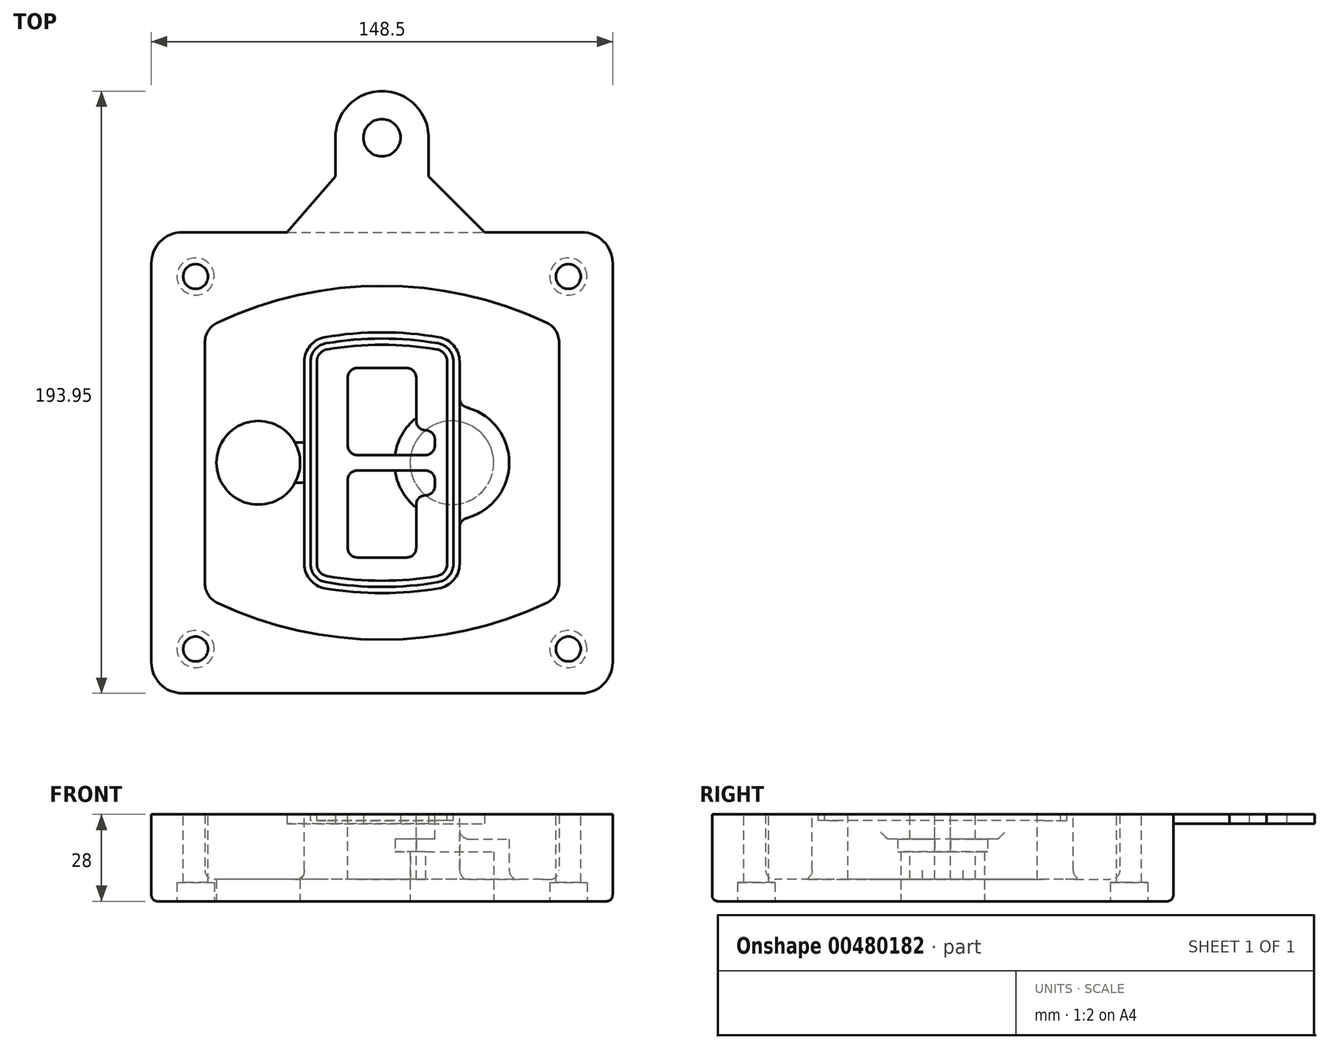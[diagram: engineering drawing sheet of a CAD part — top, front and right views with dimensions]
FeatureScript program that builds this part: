
annotation { "Feature Type Name" : "Feature", "Feature Type Description" : "" }
export const myFeature = defineFeature(function(context is Context, id is Id, definition is map)
    precondition{}
    {
        {
            var Q0;
            Q0=qCreatedBy(makeId("Top.planeOp"),FACE);
            var sketch = newSketch(context, id + "F0", { "sketchPlane" : qUnion([Q0])});
            skPoint(sketch, "E0.rect.middle", {"position": v(0, 0) * mm});
            skLineSegment(sketch, "E1.bottom", {"start": v(-64.25, -74.25) * mm, "end": v(64.25, -74.25) * mm});
            skLineSegment(sketch, "E1.top", {"start": v(-64.25, 74.25) * mm, "end": v(64.25, 74.25) * mm});
            skLineSegment(sketch, "E1.left", {"start": v(-74.25, -64.25) * mm, "end": v(-74.25, 64.25) * mm});
            skLineSegment(sketch, "E1.right", {"start": v(74.25, -64.25) * mm, "end": v(74.25, 64.25) * mm});
            skLineSegment(sketch, "E2", {"start": v(-74.25, 74.25) * mm, "end": v(74.25, -74.25) * mm, "construction": true});
            skLineSegment(sketch, "E3", {"start": v(74.25, 74.25) * mm, "end": v(-74.25, -74.25) * mm, "construction": true});
            skCircle(sketch, "E4", {"center": v(-60, 60) * mm, "radius": 4 * mm});
            skCircle(sketch, "E5", {"center": v(60, 60) * mm, "radius": 4 * mm});
            skCircle(sketch, "E6", {"center": v(60, -60) * mm, "radius": 4 * mm});
            skCircle(sketch, "E7", {"center": v(-60, -60) * mm, "radius": 4 * mm});
            skLineSegment(sketch, "E8", {"start": v(-60, 60) * mm, "end": v(60, 60) * mm, "construction": true});
            skLineSegment(sketch, "E9", {"start": v(60, 60) * mm, "end": v(60, -60) * mm, "construction": true});
            skLineSegment(sketch, "E10", {"start": v(60, -60) * mm, "end": v(-60, -60) * mm, "construction": true});
            skLineSegment(sketch, "E11", {"start": v(-60, -60) * mm, "end": v(-60, 60) * mm, "construction": true});
            skLineSegment(sketch, "E12", {"start": v(-60, 38.83) * mm, "end": v(-60, -38.83) * mm});
            skLineSegment(sketch, "E13", {"start": v(60, 38.83) * mm, "end": v(60, -38.83) * mm});
            skArc(sketch, "E14", {"start": v(54.26, 47.88) * mm, "mid": v(0, 60) * mm, "end": v(-54.26, 47.88) * mm});
            skArc(sketch, "E15", {"start": v(-54.26, -47.88) * mm, "mid": v(0, -60) * mm, "end": v(54.26, -47.88) * mm});
            skLineSegment(sketch, "E16", {"start": v(-60, 0) * mm, "end": v(60, 0) * mm, "construction": true});
            skPoint(sketch, "E17.visualSharp", {"position": v(-60, -45) * mm});
            skArc(sketch, "E17.filletArc", {"start": v(-60, -38.83) * mm, "mid": v(-58.44, -44.2) * mm, "end": v(-54.26, -47.88) * mm});
            skPoint(sketch, "E18.visualSharp", {"position": v(-60, 45) * mm});
            skArc(sketch, "E18.filletArc", {"start": v(-54.26, 47.88) * mm, "mid": v(-58.44, 44.2) * mm, "end": v(-60, 38.83) * mm});
            skPoint(sketch, "E19.visualSharp", {"position": v(60, 45) * mm});
            skArc(sketch, "E19.filletArc", {"start": v(60, 38.83) * mm, "mid": v(58.44, 44.2) * mm, "end": v(54.26, 47.88) * mm});
            skPoint(sketch, "E20.visualSharp", {"position": v(60, -45) * mm});
            skArc(sketch, "E20.filletArc", {"start": v(54.26, -47.88) * mm, "mid": v(58.44, -44.2) * mm, "end": v(60, -38.83) * mm});
            skPoint(sketch, "E21.visualSharp", {"position": v(-74.25, 74.25) * mm});
            skArc(sketch, "E21.filletArc", {"start": v(-64.25, 74.25) * mm, "mid": v(-71.32, 71.32) * mm, "end": v(-74.25, 64.25) * mm});
            skPoint(sketch, "E22.visualSharp", {"position": v(74.25, 74.25) * mm});
            skArc(sketch, "E22.filletArc", {"start": v(74.25, 64.25) * mm, "mid": v(71.32, 71.32) * mm, "end": v(64.25, 74.25) * mm});
            skPoint(sketch, "E23.visualSharp", {"position": v(74.25, -74.25) * mm});
            skArc(sketch, "E23.filletArc", {"start": v(64.25, -74.25) * mm, "mid": v(71.32, -71.32) * mm, "end": v(74.25, -64.25) * mm});
            skPoint(sketch, "E24.visualSharp", {"position": v(-74.25, -74.25) * mm});
            skArc(sketch, "E24.filletArc", {"start": v(-74.25, -64.25) * mm, "mid": v(-71.32, -71.32) * mm, "end": v(-64.25, -74.25) * mm});
            skArc(sketch, "E25.0", {"start": v(57, 38.83) * mm, "mid": v(55.9, 42.58) * mm, "end": v(52.98, 45.17) * mm});
            skLineSegment(sketch, "E25.1", {"start": v(57, 38.83) * mm, "end": v(57, -38.83) * mm});
            skArc(sketch, "E25.2", {"start": v(52.98, -45.17) * mm, "mid": v(55.9, -42.58) * mm, "end": v(57, -38.83) * mm});
            skArc(sketch, "E25.3", {"start": v(-52.98, -45.17) * mm, "mid": v(0, -57) * mm, "end": v(52.98, -45.17) * mm});
            skArc(sketch, "E25.4", {"start": v(-57, -38.83) * mm, "mid": v(-55.9, -42.58) * mm, "end": v(-52.98, -45.17) * mm});
            skArc(sketch, "E25.5", {"start": v(52.98, 45.17) * mm, "mid": v(0, 57) * mm, "end": v(-52.98, 45.17) * mm});
            skLineSegment(sketch, "E25.6", {"start": v(-57, 38.83) * mm, "end": v(-57, -38.83) * mm});
            skArc(sketch, "E25.7", {"start": v(-52.98, 45.17) * mm, "mid": v(-55.9, 42.58) * mm, "end": v(-57, 38.83) * mm});
            skArc(sketch, "E26.0", {"start": v(-55.96, 51.5) * mm, "mid": v(-61.82, 46.33) * mm, "end": v(-64, 38.83) * mm});
            skArc(sketch, "E26.1", {"start": v(55.96, 51.5) * mm, "mid": v(0, 64) * mm, "end": v(-55.96, 51.5) * mm});
            skArc(sketch, "E26.2", {"start": v(64, 38.83) * mm, "mid": v(61.82, 46.33) * mm, "end": v(55.96, 51.5) * mm});
            skLineSegment(sketch, "E26.3", {"start": v(64, 38.83) * mm, "end": v(64, -38.83) * mm});
            skArc(sketch, "E26.4", {"start": v(55.96, -51.5) * mm, "mid": v(61.82, -46.33) * mm, "end": v(64, -38.83) * mm});
            skLineSegment(sketch, "E26.5", {"start": v(-64, 38.83) * mm, "end": v(-64, -38.83) * mm});
            skArc(sketch, "E26.6", {"start": v(-55.96, -51.5) * mm, "mid": v(0, -64) * mm, "end": v(55.96, -51.5) * mm});
            skArc(sketch, "E26.7", {"start": v(-64, -38.83) * mm, "mid": v(-61.82, -46.33) * mm, "end": v(-55.96, -51.5) * mm});
            skSolve(sketch);
        }
        {
            var Q0;
            Q0=makeQuery(id+"F0.imprint","IMPRINT",FACE,{"disambiguationData":[TD([[makeQuery(id+"F0.imprint","IMPRINT",EDGE,{"derivedFrom":sQuery(id+"F0.wireOp",EDGE,"E1.bottom")}),1.0]])]});
            var Q1;
            Q1=makeQuery(id+"F0.imprint","IMPRINT",FACE,{"disambiguationData":[TD([[makeQuery(id+"F0.imprint","IMPRINT",EDGE,{"derivedFrom":sQuery(id+"F0.wireOp",EDGE,"E12")}),1.0]])]});
            var Q2;
            Q2=makeQuery(id+"F0.imprint","IMPRINT",FACE,{"disambiguationData":[TD([[makeQuery(id+"F0.imprint","IMPRINT",EDGE,{"derivedFrom":sQuery(id+"F0.wireOp",EDGE,"E25.0")}),1.0]])]});
            var Q3;
            Q3=makeQuery(id+"F0.imprint","IMPRINT",FACE,{"disambiguationData":[TD([[makeQuery(id+"F0.imprint","IMPRINT",EDGE,{"derivedFrom":sQuery(id+"F0.wireOp",EDGE,"E12")}),-1.0]])]});
            extrude(context, id + "F1", {"entities" : qUnion([Q0, Q1, Q2, Q3]), "oppositeDirection" : true, "depth" : 25 * mm});
        }
        {
            var Q0;
            Q0=makeQuery(id+"F0.imprint","IMPRINT",FACE,{"disambiguationData":[TD([[makeQuery(id+"F0.imprint","IMPRINT",EDGE,{"derivedFrom":sQuery(id+"F0.wireOp",EDGE,"E12")}),1.0]])]});
            extrude(context, id + "F2", {"entities" : qUnion([Q0]), "operationType" : NewBodyOperationType.ADD, "depth" : 3 * mm});
        }
        {
            var Q0;
            Q0=makeQuery(id+"F0.imprint","IMPRINT",FACE,{"disambiguationData":[TD([[makeQuery(id+"F0.imprint","IMPRINT",EDGE,{"derivedFrom":sQuery(id+"F0.wireOp",EDGE,"E25.0")}),1.0]])]});
            extrude(context, id + "F3", {"entities" : qUnion([Q0]), "operationType" : NewBodyOperationType.REMOVE, "oppositeDirection" : true, "depth" : 18 * mm});
        }
        {
            var Q0;
            Q0=makeQuery(id+"F2.opExtrude","CAP_FACE",FACE,{"disambiguationData":[OSD([sQuery(id+"F0.wireOp",EDGE,"E12"),sQuery(id+"F0.wireOp",EDGE,"E13"),sQuery(id+"F0.wireOp",EDGE,"E14"),sQuery(id+"F0.wireOp",EDGE,"E15"),sQuery(id+"F0.wireOp",EDGE,"E17.filletArc"),sQuery(id+"F0.wireOp",EDGE,"E18.filletArc"),sQuery(id+"F0.wireOp",EDGE,"E19.filletArc"),sQuery(id+"F0.wireOp",EDGE,"E20.filletArc"),sQuery(id+"F0.wireOp",EDGE,"E25.0"),sQuery(id+"F0.wireOp",EDGE,"E25.1"),sQuery(id+"F0.wireOp",EDGE,"E25.2"),sQuery(id+"F0.wireOp",EDGE,"E25.3"),sQuery(id+"F0.wireOp",EDGE,"E25.4"),sQuery(id+"F0.wireOp",EDGE,"E25.5"),sQuery(id+"F0.wireOp",EDGE,"E25.6"),sQuery(id+"F0.wireOp",EDGE,"E25.7")])],"isStart":false});
            var sketch = newSketch(context, id + "F4", { "sketchPlane" : qUnion([Q0])});
            skArc(sketch, "E27.0", {"start": v(-18.34, -40.45) * mm, "mid": v(0, -42) * mm, "end": v(18.34, -40.45) * mm});
            skArc(sketch, "E28.0", {"start": v(18.34, 40.45) * mm, "mid": v(0, 42) * mm, "end": v(-18.34, 40.45) * mm});
            skLineSegment(sketch, "E29", {"start": v(-25, 32.57) * mm, "end": v(-25, -32.57) * mm});
            skLineSegment(sketch, "E30", {"start": v(25, 32.57) * mm, "end": v(25, -32.57) * mm});
            skLineSegment(sketch, "E31", {"start": v(-25, 39.1) * mm, "end": v(25, 39.1) * mm, "construction": true});
            skLineSegment(sketch, "E32", {"start": v(-25, -39.1) * mm, "end": v(25, -39.1) * mm, "construction": true});
            skPoint(sketch, "E33.visualSharp", {"position": v(-25, 39.1) * mm});
            skArc(sketch, "E33.filletArc", {"start": v(-18.34, 40.45) * mm, "mid": v(-23.11, 37.73) * mm, "end": v(-25, 32.57) * mm});
            skPoint(sketch, "E34.visualSharp", {"position": v(25, 39.1) * mm});
            skArc(sketch, "E34.filletArc", {"start": v(25, 32.57) * mm, "mid": v(23.11, 37.73) * mm, "end": v(18.34, 40.45) * mm});
            skPoint(sketch, "E35.visualSharp", {"position": v(25, -39.1) * mm});
            skArc(sketch, "E35.filletArc", {"start": v(18.34, -40.45) * mm, "mid": v(23.11, -37.73) * mm, "end": v(25, -32.57) * mm});
            skPoint(sketch, "E36.visualSharp", {"position": v(-25, -39.1) * mm});
            skArc(sketch, "E36.filletArc", {"start": v(-25, -32.57) * mm, "mid": v(-23.11, -37.73) * mm, "end": v(-18.34, -40.45) * mm});
            skArc(sketch, "E37.0", {"start": v(52.98, 45.17) * mm, "mid": v(0, 57) * mm, "end": v(-52.98, 45.17) * mm});
            skArc(sketch, "E37.1", {"start": v(-52.98, 45.17) * mm, "mid": v(-55.9, 42.58) * mm, "end": v(-57, 38.83) * mm});
            skLineSegment(sketch, "E37.2", {"start": v(-57, 38.83) * mm, "end": v(-57, -38.83) * mm});
            skArc(sketch, "E37.3", {"start": v(-57, -38.83) * mm, "mid": v(-55.9, -42.58) * mm, "end": v(-52.98, -45.17) * mm});
            skArc(sketch, "E37.4", {"start": v(-52.98, -45.17) * mm, "mid": v(0, -57) * mm, "end": v(52.98, -45.17) * mm});
            skArc(sketch, "E37.5", {"start": v(52.98, -45.17) * mm, "mid": v(55.9, -42.58) * mm, "end": v(57, -38.83) * mm});
            skLineSegment(sketch, "E37.6", {"start": v(57, 38.83) * mm, "end": v(57, -38.83) * mm});
            skArc(sketch, "E37.7", {"start": v(57, 38.83) * mm, "mid": v(55.9, 42.58) * mm, "end": v(52.98, 45.17) * mm});
            skLineSegment(sketch, "E38.0", {"start": v(23, 32.57) * mm, "end": v(23, -32.57) * mm});
            skArc(sketch, "E38.1", {"start": v(18, -38.48) * mm, "mid": v(21.58, -36.44) * mm, "end": v(23, -32.57) * mm});
            skArc(sketch, "E38.2", {"start": v(-18, -38.48) * mm, "mid": v(0, -40) * mm, "end": v(18, -38.48) * mm});
            skArc(sketch, "E38.3", {"start": v(-23, -32.57) * mm, "mid": v(-21.58, -36.44) * mm, "end": v(-18, -38.48) * mm});
            skLineSegment(sketch, "E38.4", {"start": v(-23, 32.57) * mm, "end": v(-23, -32.57) * mm});
            skArc(sketch, "E38.5", {"start": v(23, 32.57) * mm, "mid": v(21.58, 36.44) * mm, "end": v(18, 38.48) * mm});
            skArc(sketch, "E38.6", {"start": v(-18, 38.48) * mm, "mid": v(-21.58, 36.44) * mm, "end": v(-23, 32.57) * mm});
            skArc(sketch, "E38.7", {"start": v(18, 38.48) * mm, "mid": v(0, 40) * mm, "end": v(-18, 38.48) * mm});
            skArc(sketch, "E39.0", {"start": v(21, 32.57) * mm, "mid": v(20.06, 35.15) * mm, "end": v(17.67, 36.5) * mm});
            skLineSegment(sketch, "E39.1", {"start": v(21, 32.57) * mm, "end": v(21, -32.57) * mm});
            skArc(sketch, "E39.2", {"start": v(17.67, -36.5) * mm, "mid": v(20.06, -35.15) * mm, "end": v(21, -32.57) * mm});
            skArc(sketch, "E39.3", {"start": v(-17.67, -36.5) * mm, "mid": v(0, -38) * mm, "end": v(17.67, -36.5) * mm});
            skArc(sketch, "E39.4", {"start": v(-21, -32.57) * mm, "mid": v(-20.06, -35.15) * mm, "end": v(-17.67, -36.5) * mm});
            skArc(sketch, "E39.5", {"start": v(17.67, 36.5) * mm, "mid": v(0, 38) * mm, "end": v(-17.67, 36.5) * mm});
            skLineSegment(sketch, "E39.6", {"start": v(-21, 32.57) * mm, "end": v(-21, -32.57) * mm});
            skArc(sketch, "E39.7", {"start": v(-17.67, 36.5) * mm, "mid": v(-20.06, 35.15) * mm, "end": v(-21, 32.57) * mm});
            skLineSegment(sketch, "E40", {"start": v(-25, 0) * mm, "end": v(25, 0) * mm, "construction": true});
            skLineSegment(sketch, "E41", {"start": v(-11, 5.5) * mm, "end": v(-11, 27.5) * mm});
            skLineSegment(sketch, "E42", {"start": v(-8, 30.5) * mm, "end": v(8, 30.5) * mm});
            skLineSegment(sketch, "E43", {"start": v(11, 27.5) * mm, "end": v(11, 13.5) * mm});
            skLineSegment(sketch, "E44", {"start": v(14, 10.5) * mm, "end": v(14, 10.5) * mm});
            skLineSegment(sketch, "E45", {"start": v(17, 7.5) * mm, "end": v(17, 5.5) * mm});
            skLineSegment(sketch, "E46", {"start": v(14, 2.5) * mm, "end": v(-8, 2.5) * mm});
            skPoint(sketch, "E47.visualSharp", {"position": v(-11, 30.5) * mm});
            skArc(sketch, "E47.filletArc", {"start": v(-8, 30.5) * mm, "mid": v(-10.12, 29.62) * mm, "end": v(-11, 27.5) * mm});
            skPoint(sketch, "E48.visualSharp", {"position": v(11, 30.5) * mm});
            skArc(sketch, "E48.filletArc", {"start": v(11, 27.5) * mm, "mid": v(10.12, 29.62) * mm, "end": v(8, 30.5) * mm});
            skPoint(sketch, "E49.visualSharp", {"position": v(11, 10.5) * mm});
            skArc(sketch, "E49.filletArc", {"start": v(11, 13.5) * mm, "mid": v(11.88, 11.38) * mm, "end": v(14, 10.5) * mm});
            skPoint(sketch, "E50.visualSharp", {"position": v(17, 10.5) * mm});
            skArc(sketch, "E50.filletArc", {"start": v(17, 7.5) * mm, "mid": v(16.12, 9.62) * mm, "end": v(14, 10.5) * mm});
            skPoint(sketch, "E51.visualSharp", {"position": v(17, 2.5) * mm});
            skArc(sketch, "E51.filletArc", {"start": v(14, 2.5) * mm, "mid": v(16.12, 3.38) * mm, "end": v(17, 5.5) * mm});
            skPoint(sketch, "E52.visualSharp", {"position": v(-11, 2.5) * mm});
            skArc(sketch, "E52.filletArc", {"start": v(-11, 5.5) * mm, "mid": v(-10.12, 3.38) * mm, "end": v(-8, 2.5) * mm});
            skLineSegment(sketch, "E53.0.MirrorCS", {"start": v(14, -2.5) * mm, "end": v(-8, -2.5) * mm});
            skArc(sketch, "E54.0.MirrorCS", {"start": v(-11, -5.5) * mm, "mid": v(-10.12, -3.38) * mm, "end": v(-8, -2.5) * mm});
            skLineSegment(sketch, "E55.0.MirrorCS", {"start": v(-11, -5.5) * mm, "end": v(-11, -27.5) * mm});
            skArc(sketch, "E56.0.MirrorCS", {"start": v(-8, -30.5) * mm, "mid": v(-10.12, -29.62) * mm, "end": v(-11, -27.5) * mm});
            skLineSegment(sketch, "E57.0.MirrorCS", {"start": v(-8, -30.5) * mm, "end": v(8, -30.5) * mm});
            skArc(sketch, "E58.0.MirrorCS", {"start": v(11, -27.5) * mm, "mid": v(10.12, -29.62) * mm, "end": v(8, -30.5) * mm});
            skLineSegment(sketch, "E59.0.MirrorCS", {"start": v(11, -27.5) * mm, "end": v(11, -13.5) * mm});
            skArc(sketch, "E60.0.MirrorCS", {"start": v(11, -13.5) * mm, "mid": v(11.88, -11.38) * mm, "end": v(14, -10.5) * mm});
            skArc(sketch, "E61.0.MirrorCS", {"start": v(17, -7.5) * mm, "mid": v(16.12, -9.62) * mm, "end": v(14, -10.5) * mm});
            skLineSegment(sketch, "E62.0.MirrorCS", {"start": v(17, -7.5) * mm, "end": v(17, -5.5) * mm});
            skArc(sketch, "E63.0.MirrorCS", {"start": v(14, -2.5) * mm, "mid": v(16.12, -3.38) * mm, "end": v(17, -5.5) * mm});
            skSolve(sketch);
        }
        {
            var Q0;
            Q0=makeQuery(id+"F4.imprint","IMPRINT",FACE,{"disambiguationData":[TD([[makeQuery(id+"F4.imprint","IMPRINT",EDGE,{"derivedFrom":sQuery(id+"F4.wireOp",EDGE,"E27.0")}),1.0]])]});
            var Q1;
            Q1=makeQuery(id+"F4.imprint","IMPRINT",FACE,{"disambiguationData":[TD([[makeQuery(id+"F4.imprint","IMPRINT",EDGE,{"derivedFrom":sQuery(id+"F4.wireOp",EDGE,"E38.0")}),-1.0]])]});
            var Q2;
            Q2=makeQuery(id+"F4.imprint","IMPRINT",FACE,{"disambiguationData":[TD([[makeQuery(id+"F4.imprint","IMPRINT",EDGE,{"derivedFrom":sQuery(id+"F4.wireOp",EDGE,"E39.0")}),1.0]])]});
            extrude(context, id + "F5", {"entities" : qUnion([Q0, Q1, Q2]), "operationType" : NewBodyOperationType.ADD, "endBound" : BoundingType.UP_TO_NEXT, "oppositeDirection" : true, "depth" : 25 * mm});
        }
        {
            var Q0;
            Q0=makeQuery(id+"F4.imprint","IMPRINT",FACE,{"disambiguationData":[TD([[makeQuery(id+"F4.imprint","IMPRINT",EDGE,{"derivedFrom":sQuery(id+"F4.wireOp",EDGE,"E38.0")}),-1.0]])]});
            extrude(context, id + "F6", {"entities" : qUnion([Q0]), "operationType" : NewBodyOperationType.REMOVE, "oppositeDirection" : true, "depth" : 2 * mm});
        }
        {
            var Q0;
            Q0=makeQuery(id+"F1.opExtrude","CAP_FACE",FACE,{"disambiguationData":[OSD([sQuery(id+"F0.wireOp",EDGE,"E1.bottom"),sQuery(id+"F0.wireOp",EDGE,"E1.top"),sQuery(id+"F0.wireOp",EDGE,"E1.left"),sQuery(id+"F0.wireOp",EDGE,"E1.right"),sQuery(id+"F0.wireOp",EDGE,"E4"),sQuery(id+"F0.wireOp",EDGE,"E5"),sQuery(id+"F0.wireOp",EDGE,"E6"),sQuery(id+"F0.wireOp",EDGE,"E7"),sQuery(id+"F0.wireOp",EDGE,"E21.filletArc"),sQuery(id+"F0.wireOp",EDGE,"E22.filletArc"),sQuery(id+"F0.wireOp",EDGE,"E23.filletArc"),sQuery(id+"F0.wireOp",EDGE,"E24.filletArc")])],"isStart":false});
            var sketch = newSketch(context, id + "F7", { "sketchPlane" : qUnion([Q0])});
            skCircle(sketch, "E64", {"center": v(22.5, 0) * mm, "radius": 13.47 * mm});
            skCircle(sketch, "E65", {"center": v(-39.81, 0) * mm, "radius": 13.47 * mm});
            skLineSegment(sketch, "E66", {"start": v(74.25, 0) * mm, "end": v(-74.25, 0) * mm});
            skCircle(sketch, "E67", {"center": v(22.5, 0) * mm, "radius": 18.47 * mm});
            skCircle(sketch, "E68", {"center": v(60, -60) * mm, "radius": 6 * mm});
            skCircle(sketch, "E69", {"center": v(-60, -60) * mm, "radius": 6 * mm});
            skCircle(sketch, "E70", {"center": v(-60, 60) * mm, "radius": 6 * mm});
            skCircle(sketch, "E71", {"center": v(60, 60) * mm, "radius": 6 * mm});
            skSolve(sketch);
        }
        {
            var Q0;
            {var subQ1=sQuery(id+"F7.wireOp",EDGE,"E66");var subQ4=sQuery(id+"F7.wireOp",EDGE,"E64");var subQ6=makeQuery(id+"F7.imprint","INTERSECT",VERTEX,{"disambiguationData":[OD(0.0)],"derivedFrom":[subQ4,subQ1]});Q0=makeQuery(id+"F7.imprint","IMPRINT",FACE,{"disambiguationData":[TD([[makeQuery(id+"F7.imprint","IMPRINT",EDGE,{"disambiguationData":[TD([[subQ6,-1.0]])],"derivedFrom":subQ4}),-1.0]])]});}
            var Q1;
            {var subQ0=sQuery(id+"F7.wireOp",EDGE,"E66");var subQ1=sQuery(id+"F7.wireOp",EDGE,"E64");var subQ3=makeQuery(id+"F7.imprint","INTERSECT",VERTEX,{"disambiguationData":[OD(0.0)],"derivedFrom":[subQ1,subQ0]});Q1=makeQuery(id+"F7.imprint","IMPRINT",FACE,{"disambiguationData":[TD([[makeQuery(id+"F7.imprint","IMPRINT",EDGE,{"disambiguationData":[TD([[subQ3,-1.0]])],"derivedFrom":subQ1}),1.0]])]});}
            var Q2;
            {var subQ0=sQuery(id+"F7.wireOp",EDGE,"E66");var subQ1=sQuery(id+"F7.wireOp",EDGE,"E64");var subQ3=makeQuery(id+"F7.imprint","INTERSECT",VERTEX,{"disambiguationData":[OD(0.0)],"derivedFrom":[subQ1,subQ0]});Q2=makeQuery(id+"F7.imprint","IMPRINT",FACE,{"disambiguationData":[TD([[makeQuery(id+"F7.imprint","IMPRINT",EDGE,{"disambiguationData":[TD([[subQ3,1.0]])],"derivedFrom":subQ1}),1.0]])]});}
            var Q3;
            {var subQ1=sQuery(id+"F7.wireOp",EDGE,"E66");var subQ4=sQuery(id+"F7.wireOp",EDGE,"E64");var subQ6=makeQuery(id+"F7.imprint","INTERSECT",VERTEX,{"disambiguationData":[OD(0.0)],"derivedFrom":[subQ4,subQ1]});Q3=makeQuery(id+"F7.imprint","IMPRINT",FACE,{"disambiguationData":[TD([[makeQuery(id+"F7.imprint","IMPRINT",EDGE,{"disambiguationData":[TD([[subQ6,1.0]])],"derivedFrom":subQ4}),-1.0]])]});}
            extrude(context, id + "F8", {"entities" : qUnion([Q0, Q1, Q2, Q3]), "operationType" : NewBodyOperationType.ADD, "oppositeDirection" : true, "depth" : 20 * mm});
        }
        {
            var Q0;
            {var subQ0=sQuery(id+"F7.wireOp",EDGE,"E66");var subQ1=sQuery(id+"F7.wireOp",EDGE,"E64");var subQ3=makeQuery(id+"F7.imprint","INTERSECT",VERTEX,{"disambiguationData":[OD(0.0)],"derivedFrom":[subQ1,subQ0]});Q0=makeQuery(id+"F7.imprint","IMPRINT",FACE,{"disambiguationData":[TD([[makeQuery(id+"F7.imprint","IMPRINT",EDGE,{"disambiguationData":[TD([[subQ3,-1.0]])],"derivedFrom":subQ1}),1.0]])]});}
            var Q1;
            {var subQ0=sQuery(id+"F7.wireOp",EDGE,"E66");var subQ1=sQuery(id+"F7.wireOp",EDGE,"E64");var subQ3=makeQuery(id+"F7.imprint","INTERSECT",VERTEX,{"disambiguationData":[OD(0.0)],"derivedFrom":[subQ1,subQ0]});Q1=makeQuery(id+"F7.imprint","IMPRINT",FACE,{"disambiguationData":[TD([[makeQuery(id+"F7.imprint","IMPRINT",EDGE,{"disambiguationData":[TD([[subQ3,1.0]])],"derivedFrom":subQ1}),1.0]])]});}
            extrude(context, id + "F9", {"entities" : qUnion([Q0, Q1]), "operationType" : NewBodyOperationType.REMOVE, "oppositeDirection" : true, "depth" : 16 * mm});
        }
        {
            var Q0;
            {var subQ0=sQuery(id+"F7.wireOp",EDGE,"E66");var subQ1=sQuery(id+"F7.wireOp",EDGE,"E65");var subQ3=makeQuery(id+"F7.imprint","INTERSECT",VERTEX,{"disambiguationData":[OD(0.0)],"derivedFrom":[subQ1,subQ0]});Q0=makeQuery(id+"F7.imprint","IMPRINT",FACE,{"disambiguationData":[TD([[makeQuery(id+"F7.imprint","IMPRINT",EDGE,{"disambiguationData":[TD([[subQ3,-1.0]])],"derivedFrom":subQ1}),1.0]])]});}
            var Q1;
            {var subQ0=sQuery(id+"F7.wireOp",EDGE,"E66");var subQ1=sQuery(id+"F7.wireOp",EDGE,"E65");var subQ3=makeQuery(id+"F7.imprint","INTERSECT",VERTEX,{"disambiguationData":[OD(0.0)],"derivedFrom":[subQ1,subQ0]});Q1=makeQuery(id+"F7.imprint","IMPRINT",FACE,{"disambiguationData":[TD([[makeQuery(id+"F7.imprint","IMPRINT",EDGE,{"disambiguationData":[TD([[subQ3,1.0]])],"derivedFrom":subQ1}),1.0]])]});}
            extrude(context, id + "F10", {"entities" : qUnion([Q0, Q1]), "operationType" : NewBodyOperationType.REMOVE, "oppositeDirection" : true, "depth" : 25 * mm});
        }
        {
            var Q0;
            Q0=makeQuery(id+"F7.imprint","IMPRINT",FACE,{"disambiguationData":[TD([[makeQuery(id+"F7.imprint","IMPRINT",EDGE,{"derivedFrom":sQuery(id+"F7.wireOp",EDGE,"E68")}),1.0]])]});
            var Q1;
            Q1=makeQuery(id+"F7.imprint","IMPRINT",FACE,{"disambiguationData":[TD([[makeQuery(id+"F7.imprint","IMPRINT",EDGE,{"derivedFrom":makeQuery(id+"F1.opExtrude","CAP_EDGE",EDGE,{"disambiguationData":[OSD([sQuery(id+"F0.wireOp",EDGE,"E5")])],"isStart":false})}),-1.0]])]});
            var Q2;
            Q2=makeQuery(id+"F7.imprint","IMPRINT",FACE,{"disambiguationData":[TD([[makeQuery(id+"F7.imprint","IMPRINT",EDGE,{"derivedFrom":sQuery(id+"F7.wireOp",EDGE,"E69")}),1.0]])]});
            var Q3;
            Q3=makeQuery(id+"F7.imprint","IMPRINT",FACE,{"disambiguationData":[TD([[makeQuery(id+"F7.imprint","IMPRINT",EDGE,{"derivedFrom":makeQuery(id+"F1.opExtrude","CAP_EDGE",EDGE,{"disambiguationData":[OSD([sQuery(id+"F0.wireOp",EDGE,"E4")])],"isStart":false})}),-1.0]])]});
            var Q4;
            Q4=makeQuery(id+"F7.imprint","IMPRINT",FACE,{"disambiguationData":[TD([[makeQuery(id+"F7.imprint","IMPRINT",EDGE,{"derivedFrom":sQuery(id+"F7.wireOp",EDGE,"E70")}),1.0]])]});
            var Q5;
            Q5=makeQuery(id+"F7.imprint","IMPRINT",FACE,{"disambiguationData":[TD([[makeQuery(id+"F7.imprint","IMPRINT",EDGE,{"derivedFrom":makeQuery(id+"F1.opExtrude","CAP_EDGE",EDGE,{"disambiguationData":[OSD([sQuery(id+"F0.wireOp",EDGE,"E7")])],"isStart":false})}),-1.0]])]});
            var Q6;
            Q6=makeQuery(id+"F7.imprint","IMPRINT",FACE,{"disambiguationData":[TD([[makeQuery(id+"F7.imprint","IMPRINT",EDGE,{"derivedFrom":sQuery(id+"F7.wireOp",EDGE,"E71")}),1.0]])]});
            var Q7;
            Q7=makeQuery(id+"F7.imprint","IMPRINT",FACE,{"disambiguationData":[TD([[makeQuery(id+"F7.imprint","IMPRINT",EDGE,{"derivedFrom":makeQuery(id+"F1.opExtrude","CAP_EDGE",EDGE,{"disambiguationData":[OSD([sQuery(id+"F0.wireOp",EDGE,"E6")])],"isStart":false})}),-1.0]])]});
            extrude(context, id + "F11", {"entities" : qUnion([Q0, Q1, Q2, Q3, Q4, Q5, Q6, Q7]), "operationType" : NewBodyOperationType.REMOVE, "oppositeDirection" : true, "depth" : 6 * mm});
        }
        {
            var Q0;
            Q0=makeQuery(id+"F9.boolean.opBoolean","COPY",FACE,{"derivedFrom":makeQuery(id+"F9.opExtrude","CAP_FACE",FACE,{"disambiguationData":[OSD([sQuery(id+"F7.wireOp",EDGE,"E64")])],"isStart":false})});
            var sketch = newSketch(context, id + "F12", { "sketchPlane" : qUnion([Q0])});
            skArc(sketch, "E72.0", {"start": v(11, 14.45) * mm, "mid": v(6.45, 9.13) * mm, "end": v(4.2, 2.5) * mm});
            skArc(sketch, "E72.1", {"start": v(4.2, -2.5) * mm, "mid": v(6.45, -9.13) * mm, "end": v(11, -14.45) * mm});
            skLineSegment(sketch, "E73", {"start": v(4.2, -2.5) * mm, "end": v(14, -2.5) * mm});
            skLineSegment(sketch, "E74.0", {"start": v(14, 2.5) * mm, "end": v(4.2, 2.5) * mm});
            skArc(sketch, "E74.1", {"start": v(14, 2.5) * mm, "mid": v(16.12, 3.38) * mm, "end": v(17, 5.5) * mm});
            skLineSegment(sketch, "E74.2", {"start": v(17, 7.5) * mm, "end": v(17, 5.5) * mm});
            skArc(sketch, "E74.3", {"start": v(17, 7.5) * mm, "mid": v(16.12, 9.62) * mm, "end": v(14, 10.5) * mm});
            skArc(sketch, "E74.4", {"start": v(11, 13.5) * mm, "mid": v(11.88, 11.38) * mm, "end": v(14, 10.5) * mm});
            skLineSegment(sketch, "E74.5", {"start": v(11, 14.45) * mm, "end": v(11, 13.5) * mm});
            skLineSegment(sketch, "E74.7", {"start": v(14, -2.5) * mm, "end": v(4.2, -2.5) * mm});
            skArc(sketch, "E74.8", {"start": v(14, -2.5) * mm, "mid": v(16.12, -3.38) * mm, "end": v(17, -5.5) * mm});
            skLineSegment(sketch, "E74.9", {"start": v(17, -7.5) * mm, "end": v(17, -5.5) * mm});
            skArc(sketch, "E74.10", {"start": v(17, -7.5) * mm, "mid": v(16.12, -9.62) * mm, "end": v(14, -10.5) * mm});
            skArc(sketch, "E74.11", {"start": v(11, -13.5) * mm, "mid": v(11.88, -11.38) * mm, "end": v(14, -10.5) * mm});
            skLineSegment(sketch, "E74.12", {"start": v(11, -14.45) * mm, "end": v(11, -13.5) * mm});
            skPoint(sketch, "E75.orphan", {"position": v(11, -27.5) * mm});
            skPoint(sketch, "E76.orphan", {"position": v(-8, -2.5) * mm});
            skPoint(sketch, "E77.orphan", {"position": v(-8, 2.5) * mm});
            skPoint(sketch, "E78.orphan", {"position": v(11, 27.5) * mm});
            skSolve(sketch);
        }
        {
            var Q0;
            {var subQ7=sQuery(id+"F12.wireOp",EDGE,"E72.0");var subQ14=sQuery(id+"F12.wireOp",EDGE,"E72.1");var subQ16=sQuery(id+"F12.wireOp",EDGE,"E74.1");var subQ18=sQuery(id+"F12.wireOp",EDGE,"E74.8");Q0=qUnion([makeQuery(id+"F12.imprint","IMPRINT",FACE,{"disambiguationData":[TD([[makeQuery(id+"F12.imprint","IMPRINT",EDGE,{"derivedFrom":subQ7}),1.0]])]}),makeQuery(id+"F12.imprint","IMPRINT",FACE,{"disambiguationData":[TD([[makeQuery(id+"F12.imprint","IMPRINT",EDGE,{"derivedFrom":subQ14}),1.0]])]}),makeQuery(id+"F12.imprint","IMPRINT",FACE,{"disambiguationData":[TD([[makeQuery(id+"F12.imprint","IMPRINT",EDGE,{"derivedFrom":subQ16}),1.0]])]}),makeQuery(id+"F12.imprint","IMPRINT",FACE,{"disambiguationData":[TD([[makeQuery(id+"F12.imprint","IMPRINT",EDGE,{"derivedFrom":subQ18}),-1.0]])]})]);}
            var Q1;
            Q1=makeQuery(id+"F5.boolean.opBoolean","SPLIT",FACE,{"disambiguationData":[TD([makeQuery(id+"F5.opExtrude","SWEPT_FACE",FACE,{"disambiguationData":[OSD([sQuery(id+"F4.wireOp",EDGE,"E41")])]})])],"derivedFrom":makeQuery(id+"F3.boolean.opBoolean","COPY",FACE,{"derivedFrom":makeQuery(id+"F3.opExtrude","CAP_FACE",FACE,{"disambiguationData":[OSD([sQuery(id+"F0.wireOp",EDGE,"E25.0"),sQuery(id+"F0.wireOp",EDGE,"E25.1"),sQuery(id+"F0.wireOp",EDGE,"E25.2"),sQuery(id+"F0.wireOp",EDGE,"E25.3"),sQuery(id+"F0.wireOp",EDGE,"E25.4"),sQuery(id+"F0.wireOp",EDGE,"E25.5"),sQuery(id+"F0.wireOp",EDGE,"E25.6"),sQuery(id+"F0.wireOp",EDGE,"E25.7")])],"isStart":false})})});
            extrude(context, id + "F13", {"entities" : qUnion([Q0]), "operationType" : NewBodyOperationType.REMOVE, "endBound" : BoundingType.UP_TO_SURFACE, "endBoundEntityFace" : qUnion([Q1]), "depth" : 25 * mm});
        }
        {
            var Q0;
            Q0=makeQuery(id+"F3.boolean.opBoolean","COPY",EDGE,{"derivedFrom":makeQuery(id+"F3.opExtrude","CAP_EDGE",EDGE,{"disambiguationData":[OSD([sQuery(id+"F0.wireOp",EDGE,"E25.6")])],"isStart":false})});
            var Q1;
            Q1=makeQuery(id+"F8.boolean.opBoolean","INTERSECT",EDGE,{"derivedFrom":[makeQuery(id+"F5.opExtrude","SWEPT_FACE",FACE,{"disambiguationData":[OSD([sQuery(id+"F4.wireOp",EDGE,"E30")])]}),makeQuery(id+"F8.opExtrude","CAP_FACE",FACE,{"disambiguationData":[OSD([sQuery(id+"F7.wireOp",EDGE,"E67")])],"isStart":false})]});
            var Q2;
            Q2=makeQuery(id+"F8.boolean.opBoolean","INTERSECT",EDGE,{"disambiguationData":[OD(1.0)],"derivedFrom":[makeQuery(id+"F5.opExtrude","SWEPT_FACE",FACE,{"disambiguationData":[OSD([sQuery(id+"F4.wireOp",EDGE,"E30")])]}),makeQuery(id+"F8.opExtrude","SWEPT_FACE",FACE,{"disambiguationData":[OSD([sQuery(id+"F7.wireOp",EDGE,"E67")])]})]});
            var Q3;
            {var subQ0=sQuery(id+"F4.wireOp",EDGE,"E30");Q3=makeQuery(id+"F8.boolean.opBoolean","SPLIT",EDGE,{"disambiguationData":[TD([makeQuery(id+"F5.opExtrude","SWEPT_FACE",FACE,{"disambiguationData":[OSD([sQuery(id+"F4.wireOp",EDGE,"E35.filletArc")])]})])],"derivedFrom":makeQuery(id+"F5.opExtrude","CAP_EDGE",EDGE,{"disambiguationData":[OSD([subQ0])],"isStart":false})});}
            var Q4;
            {var subQ0=sQuery(id+"F0.wireOp",EDGE,"E25.7");var subQ1=sQuery(id+"F0.wireOp",EDGE,"E25.1");var subQ2=sQuery(id+"F0.wireOp",EDGE,"E25.6");var subQ3=sQuery(id+"F0.wireOp",EDGE,"E25.5");var subQ4=sQuery(id+"F0.wireOp",EDGE,"E25.4");var subQ5=sQuery(id+"F0.wireOp",EDGE,"E25.0");var subQ6=sQuery(id+"F0.wireOp",EDGE,"E25.2");var subQ7=sQuery(id+"F0.wireOp",EDGE,"E25.3");Q4=makeQuery(id+"F8.boolean.opBoolean","INTERSECT",EDGE,{"derivedFrom":[makeQuery(id+"F5.boolean.opBoolean","SPLIT",FACE,{"disambiguationData":[TD([makeQuery(id+"F2.opExtrude","SWEPT_FACE",FACE,{"disambiguationData":[OSD([subQ5])]})])],"derivedFrom":makeQuery(id+"F3.boolean.opBoolean","COPY",FACE,{"derivedFrom":makeQuery(id+"F3.opExtrude","CAP_FACE",FACE,{"disambiguationData":[OSD([subQ5,subQ1,subQ6,subQ7,subQ4,subQ3,subQ2,subQ0])],"isStart":false})})}),makeQuery(id+"F8.opExtrude","SWEPT_FACE",FACE,{"disambiguationData":[OSD([sQuery(id+"F7.wireOp",EDGE,"E67")])]})]});}
            var Q5;
            Q5=makeQuery(id+"F8.boolean.opBoolean","INTERSECT",EDGE,{"disambiguationData":[OD(0.0)],"derivedFrom":[makeQuery(id+"F5.opExtrude","SWEPT_FACE",FACE,{"disambiguationData":[OSD([sQuery(id+"F4.wireOp",EDGE,"E30")])]}),makeQuery(id+"F8.opExtrude","SWEPT_FACE",FACE,{"disambiguationData":[OSD([sQuery(id+"F7.wireOp",EDGE,"E67")])]})]});
            fillet(context, id + "F14", {"entities" : qUnion([Q0, Q1, Q2, Q3, Q4, Q5]), "radius" : 3 * mm, "tangentPropagation" : true, "allowEdgeOverflow" : false});
        }
        {
            var Q0;
            Q0=makeQuery(id+"F1.opExtrude","CAP_EDGE",EDGE,{"disambiguationData":[OSD([sQuery(id+"F0.wireOp",EDGE,"E1.bottom")])],"isStart":false});
            fillet(context, id + "F15", {"entities" : qUnion([Q0]), "radius" : 2 * mm, "tangentPropagation" : true, "allowEdgeOverflow" : false});
        }
        {
            var Q0;
            {var subQ0=sQuery(id+"F0.wireOp",EDGE,"E21.filletArc");var subQ1=sQuery(id+"F0.wireOp",EDGE,"E7");var subQ2=sQuery(id+"F0.wireOp",EDGE,"E6");var subQ3=sQuery(id+"F0.wireOp",EDGE,"E5");var subQ4=sQuery(id+"F0.wireOp",EDGE,"E4");var subQ5=sQuery(id+"F0.wireOp",EDGE,"E22.filletArc");var subQ6=sQuery(id+"F0.wireOp",EDGE,"E1.bottom");var subQ7=sQuery(id+"F0.wireOp",EDGE,"E1.right");var subQ8=sQuery(id+"F0.wireOp",EDGE,"E1.top");var subQ9=sQuery(id+"F0.wireOp",EDGE,"E1.left");var subQ10=sQuery(id+"F0.wireOp",EDGE,"E23.filletArc");var subQ11=sQuery(id+"F0.wireOp",EDGE,"E24.filletArc");Q0=makeQuery(id+"F2.boolean.opBoolean","SPLIT",FACE,{"disambiguationData":[TD([makeQuery(id+"F1.opExtrude","SWEPT_FACE",FACE,{"disambiguationData":[OSD([subQ6])]})])],"derivedFrom":makeQuery(id+"F1.opExtrude","CAP_FACE",FACE,{"disambiguationData":[OSD([subQ6,subQ8,subQ9,subQ7,subQ4,subQ3,subQ2,subQ1,subQ0,subQ5,subQ10,subQ11])],"isStart":true})});}
            var sketch = newSketch(context, id + "F16", { "sketchPlane" : qUnion([Q0])});
            skLineSegment(sketch, "E79", {"start": v(15, 103.8) * mm, "end": v(15, 104.25) * mm});
            skLineSegment(sketch, "E80", {"start": v(-15, 92.25) * mm, "end": v(-15, 104.25) * mm});
            skArc(sketch, "E81", {"start": v(15, 104.25) * mm, "mid": v(0, 119.7) * mm, "end": v(-15, 104.25) * mm});
            skCircle(sketch, "E82", {"center": v(0, 104.7) * mm, "radius": 6 * mm});
            skPoint(sketch, "E83", {"position": v(0, 74.25) * mm});
            skLineSegment(sketch, "E84", {"start": v(0, 104.7) * mm, "end": v(0, 74.25) * mm, "construction": true});
            skLineSegment(sketch, "E85", {"start": v(15, 103.8) * mm, "end": v(15, 92.25) * mm});
            skLineSegment(sketch, "E86", {"start": v(15, 92.25) * mm, "end": v(33, 74.25) * mm});
            skLineSegment(sketch, "E87", {"start": v(-15, 92.25) * mm, "end": v(-30.55, 74.25) * mm});
            skLineSegment(sketch, "E88.MirrorCS", {"start": v(15, -92.25) * mm, "end": v(33, -74.25) * mm});
            skLineSegment(sketch, "E89.MirrorCS", {"start": v(15, -103.8) * mm, "end": v(15, -92.25) * mm});
            skArc(sketch, "E90.MirrorCS", {"start": v(15, -104.25) * mm, "mid": v(0, -119.7) * mm, "end": v(-15, -104.25) * mm});
            skLineSegment(sketch, "E91.MirrorCS", {"start": v(-15, -92.25) * mm, "end": v(-15, -104.25) * mm});
            skCircle(sketch, "E92.MirrorC", {"center": v(0, -104.7) * mm, "radius": 6 * mm});
            skLineSegment(sketch, "E93.MirrorCS", {"start": v(-15, -92.25) * mm, "end": v(-30.55, -74.25) * mm});
            skLineSegment(sketch, "E94", {"start": v(-30.55, -74.25) * mm, "end": v(33, -74.25) * mm});
            skSolve(sketch);
        }
        {
            var Q0;
            Q0=makeQuery(id+"F16.imprint","IMPRINT",FACE,{"disambiguationData":[TD([[makeQuery(id+"F16.imprint","IMPRINT",EDGE,{"derivedFrom":sQuery(id+"F16.wireOp",EDGE,"E79")}),1.0]])]});
            var Q1;
            {var subQ5=sQuery(id+"F16.wireOp",EDGE,"E94");Q1=makeQuery(id+"F16.imprint","IMPRINT",FACE,{"disambiguationData":[TD([[makeQuery(id+"F16.imprint","IMPRINT",EDGE,{"derivedFrom":subQ5}),1.0]])]});}
            var Q2;
            Q2=makeQuery(id+"F2.opExtrude","CAP_FACE",FACE,{"disambiguationData":[OSD([sQuery(id+"F0.wireOp",EDGE,"E12"),sQuery(id+"F0.wireOp",EDGE,"E13"),sQuery(id+"F0.wireOp",EDGE,"E14"),sQuery(id+"F0.wireOp",EDGE,"E15"),sQuery(id+"F0.wireOp",EDGE,"E17.filletArc"),sQuery(id+"F0.wireOp",EDGE,"E18.filletArc"),sQuery(id+"F0.wireOp",EDGE,"E19.filletArc"),sQuery(id+"F0.wireOp",EDGE,"E20.filletArc"),sQuery(id+"F0.wireOp",EDGE,"E25.0"),sQuery(id+"F0.wireOp",EDGE,"E25.1"),sQuery(id+"F0.wireOp",EDGE,"E25.2"),sQuery(id+"F0.wireOp",EDGE,"E25.3"),sQuery(id+"F0.wireOp",EDGE,"E25.4"),sQuery(id+"F0.wireOp",EDGE,"E25.5"),sQuery(id+"F0.wireOp",EDGE,"E25.6"),sQuery(id+"F0.wireOp",EDGE,"E25.7")])],"isStart":false});
            extrude(context, id + "F17", {"entities" : qUnion([Q0, Q1]), "operationType" : NewBodyOperationType.ADD, "endBound" : BoundingType.UP_TO_SURFACE, "depth" : 25 * mm, "endBoundEntityFace" : qUnion([Q2]), "offsetDistance" : 25 * mm});
        }
    });
